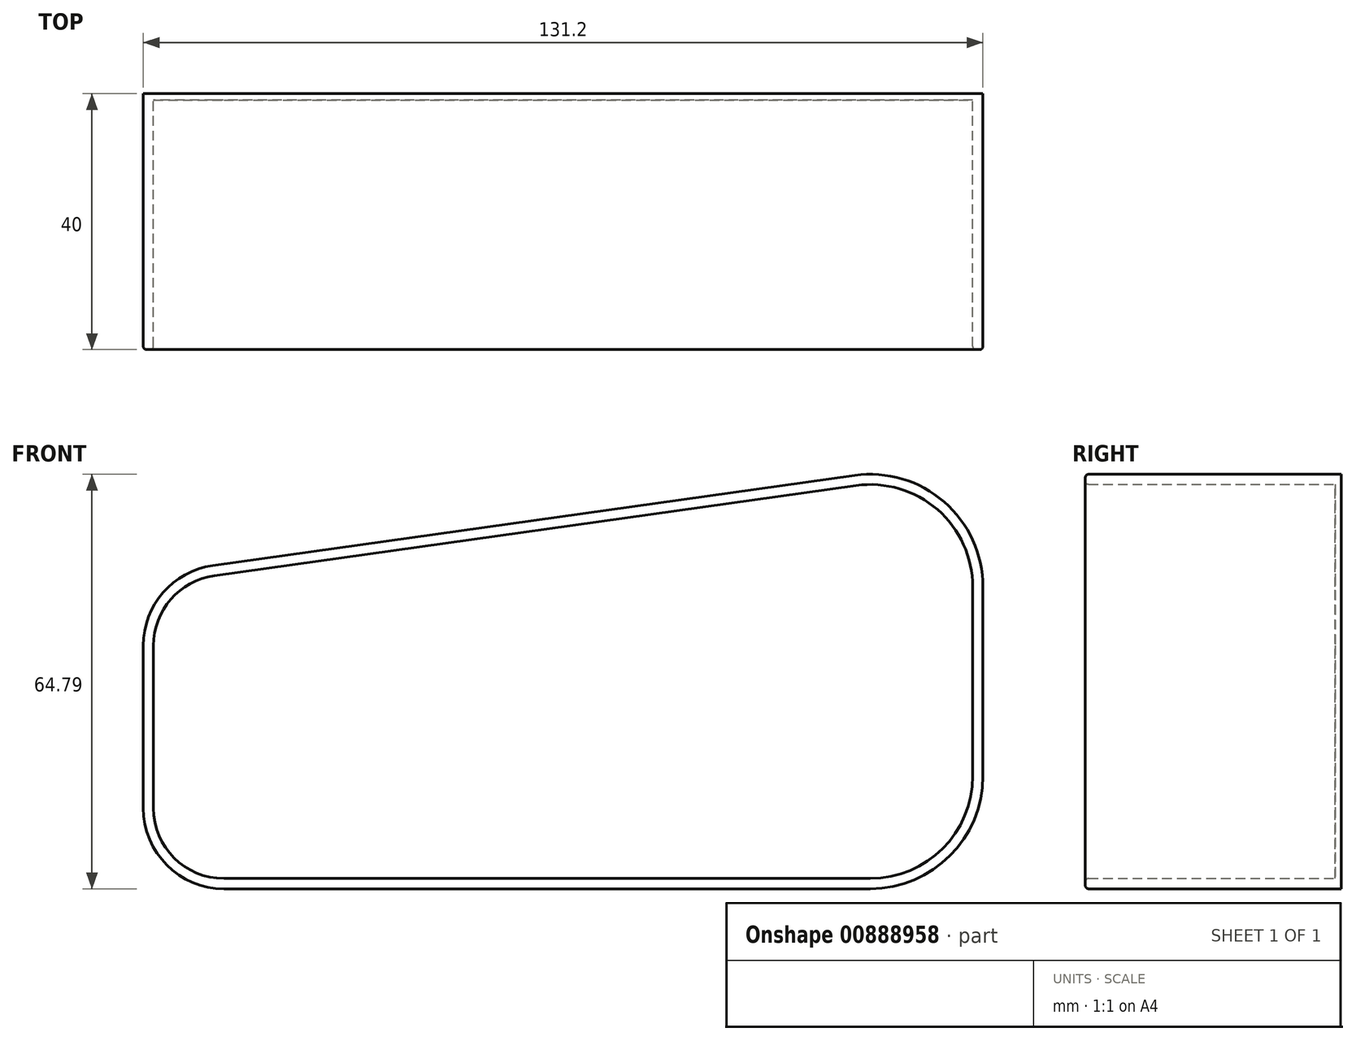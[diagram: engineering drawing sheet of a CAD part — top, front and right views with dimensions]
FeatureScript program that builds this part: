
annotation { "Feature Type Name" : "Feature", "Feature Type Description" : "" }
export const myFeature = defineFeature(function(context is Context, id is Id, definition is map)
    precondition{}
    {
        {
            var Q0;
            Q0=qCreatedBy(makeId("Front.planeOp"),FACE);
            var sketch = newSketch(context, id + "F0", { "sketchPlane" : qUnion([Q0])});
            skLineSegment(sketch, "E0", {"start": v(0, 16) * mm, "end": v(0, 45.6) * mm});
            skLineSegment(sketch, "E1", {"start": v(-18.23, 61.44) * mm, "end": v(-118.53, 47.33) * mm});
            skLineSegment(sketch, "E2", {"start": v(-128, 36.44) * mm, "end": v(-128, 11) * mm});
            skLineSegment(sketch, "E3", {"start": v(-117, 0) * mm, "end": v(-16, 0) * mm});
            skPoint(sketch, "E4.visualSharp", {"position": v(0, 64) * mm});
            skArc(sketch, "E4.filletArc", {"start": v(0, 45.6) * mm, "mid": v(-5.5, 57.67) * mm, "end": v(-18.23, 61.44) * mm});
            skPoint(sketch, "E5.visualSharp", {"position": v(0, 0) * mm});
            skArc(sketch, "E5.filletArc", {"start": v(-16, 0) * mm, "mid": v(-4.69, 4.69) * mm, "end": v(0, 16) * mm});
            skPoint(sketch, "E6.visualSharp", {"position": v(-128, 46) * mm});
            skArc(sketch, "E6.filletArc", {"start": v(-118.53, 47.33) * mm, "mid": v(-125.3, 43.65) * mm, "end": v(-128, 36.44) * mm});
            skPoint(sketch, "E7.visualSharp", {"position": v(-128, 0) * mm});
            skArc(sketch, "E7.filletArc", {"start": v(-128, 11) * mm, "mid": v(-124.78, 3.22) * mm, "end": v(-117, 0) * mm});
            skLineSegment(sketch, "E8.0", {"start": v(-117, -1.6) * mm, "end": v(-16, -1.6) * mm});
            skArc(sketch, "E8.1", {"start": v(-129.6, 11) * mm, "mid": v(-125.9, 2.1) * mm, "end": v(-117, -1.6) * mm});
            skArc(sketch, "E8.2", {"start": v(-16, -1.6) * mm, "mid": v(-3.55, 3.55) * mm, "end": v(1.6, 16) * mm});
            skLineSegment(sketch, "E8.3", {"start": v(-129.6, 36.44) * mm, "end": v(-129.6, 11) * mm});
            skLineSegment(sketch, "E8.4", {"start": v(1.6, 16) * mm, "end": v(1.6, 45.6) * mm});
            skArc(sketch, "E8.5", {"start": v(1.6, 45.6) * mm, "mid": v(-4.45, 58.88) * mm, "end": v(-18.45, 63.02) * mm});
            skLineSegment(sketch, "E8.6", {"start": v(-18.45, 63.02) * mm, "end": v(-118.75, 48.92) * mm});
            skArc(sketch, "E8.7", {"start": v(-118.75, 48.92) * mm, "mid": v(-126.5, 44.7) * mm, "end": v(-129.6, 36.44) * mm});
            skSolve(sketch);
        }
        {
            var Q0;
            Q0=makeQuery(id+"F0.imprint","IMPRINT",FACE,{"disambiguationData":[TD([[makeQuery(id+"F0.imprint","IMPRINT",EDGE,{"derivedFrom":sQuery(id+"F0.wireOp",EDGE,"E0")}),1.0]])]});
            extrude(context, id + "F1", {"entities" : qUnion([Q0]), "depth" : 1 * mm, "offsetDistance" : 25 * mm});
        }
        {
            var Q0;
            Q0 = qSketchRegion(id + "F0", true);
            extrude(context, id + "F2", {"entities" : qUnion([Q0]), "operationType" : NewBodyOperationType.ADD, "depth" : 40 * mm, "offsetDistance" : 25 * mm});
        }
        {
            var Q0;
            Q0=makeQuery(id+"F2.opExtrude","CAP_EDGE",EDGE,{"disambiguationData":[OSD([sQuery(id+"F0.wireOp",EDGE,"E8.0")])],"isStart":false});
            var Q1;
            Q1=makeQuery(id+"F2.opExtrude","CAP_EDGE",EDGE,{"disambiguationData":[OSD([sQuery(id+"F0.wireOp",EDGE,"E3")])],"isStart":false});
            fillet(context, id + "F3", {"entities" : qUnion([Q0, Q1]), "radius" : .5 * mm, "tangentPropagation" : true, "allowEdgeOverflow" : false});
        }
    });
